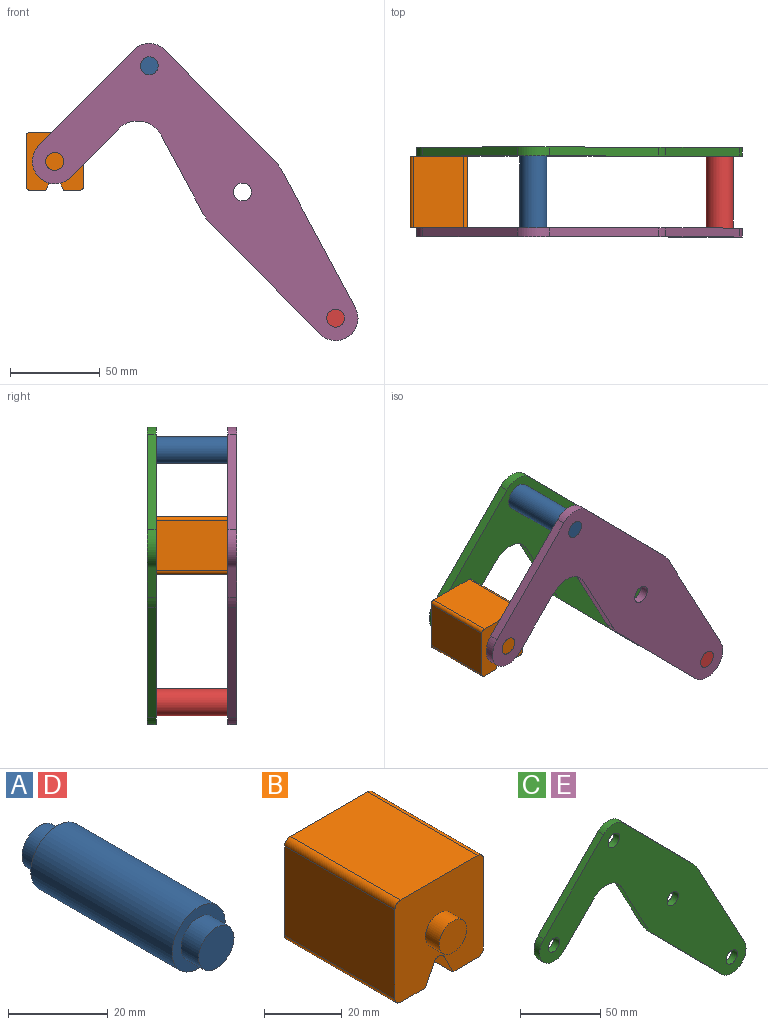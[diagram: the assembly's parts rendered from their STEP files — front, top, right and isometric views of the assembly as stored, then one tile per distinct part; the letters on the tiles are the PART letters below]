
ASSEMBLY  parts=5 mates=3
PART A: 7 faces, bbox 15x50x15 mm
  f0: cylinder r=7.5mm len=40mm, axis (0,-1,0), area 1885mm2, adj f2,f5
  f1: cylinder r=5mm len=10mm, axis (0,1,0), area 157.1mm2, adj f2,f3
  f2: plane 15x15mm, normal (0,-1,0), area 98.2mm2, adj f0,f1
  f3: plane 10x10mm, normal (0,-1,0), area 78.5mm2, adj f1
  f4: cylinder r=5mm len=10mm, axis (0,-1,0), area 157.1mm2, adj f5,f6
  f5: plane 15x15mm, normal (0,1,0), area 98.2mm2, adj f0,f4
  f6: plane 10x10mm, normal (0,1,0), area 78.5mm2, adj f4
PART B: 18 faces, bbox 32.1x50x32.1 mm
  f0: plane 40x28.08mm, normal (1,0,0), area 1123.1mm2, adj f4,f10,f13,f14
  f1: plane 40x9.04mm, normal (0,0,-1), area 361.6mm2, adj f2,f4,f10,f14
  f2: plane 40x6.42mm, normal (-0.89,0,-0.45), area 287.2mm2, adj f1,f4,f10,f15
  f3: plane 40x6.42mm, normal (0.89,0,-0.45), area 287.2mm2, adj f4,f5,f10,f15
  f4: plane 32.08x32.08mm, normal (0,-1,0), area 900.6mm2, adj f0,f1,f2,f3,f5,f6,f7,f9
  f5: plane 40x9.04mm, normal (0,0,-1), area 361.6mm2, adj f3,f4,f10,f16
  f6: plane 40x28.08mm, normal (0,0,1), area 1123.1mm2, adj f4,f10,f13,f17
  f7: plane 40x28.08mm, normal (-1,0,0), area 1123.1mm2, adj f4,f10,f16,f17
  f8: plane 10x10mm, normal (0,-1,0), area 78.5mm2, adj f9
  f9: cylinder r=5mm len=10mm, axis (0,1,0), area 157.1mm2, adj f4,f8
  f10: plane 32.08x32.08mm, normal (0,1,0), area 900.6mm2, adj f0,f1,f2,f3,f5,f6,f7,f12
  f11: plane 10x10mm, normal (0,1,0), area 78.5mm2, adj f12
  f12: cylinder r=5mm len=10mm, axis (0,-1,0), area 157.1mm2, adj f10,f11
  f13: cylinder r=2mm len=40mm, axis (0,1,0), area 125.7mm2, adj f0,f4,f6,f10
  f14: cylinder r=2mm len=40mm, axis (0,-1,0), area 125.7mm2, adj f0,f1,f4,f10
  f15: cylinder r=2mm len=40mm, axis (0,1,0), area 177.1mm2, adj f2,f3,f4,f10
  f16: cylinder r=2mm len=40mm, axis (0,1,0), area 125.7mm2, adj f4,f5,f7,f10
  f17: cylinder r=2mm len=40mm, axis (0,-1,0), area 125.7mm2, adj f4,f6,f7,f10
PART C: 18 faces, bbox 181.7x5x165.8 mm
  f0: plane 43.49x23.35mm, normal (-0.88,0,-0.47), area 246.8mm2, adj f1,f14,f16,f17
  f1: cylinder r=25mm len=5.75mm, axis (0,1,0), area 35.8mm2, adj f0,f2,f16,f17
  f2: plane 61.6x60.87mm, normal (-0.71,0,-0.7), area 433mm2, adj f1,f3,f16,f17
  f3: cylinder r=12.5mm len=21.39mm, axis (0,1,0), area 178.4mm2, adj f2,f4,f16,f17
  f4: plane 76.3x40.96mm, normal (0.88,0,0.47), area 433mm2, adj f3,f5,f16,f17
  f5: cylinder r=25mm len=5.75mm, axis (0,1,0), area 35.8mm2, adj f4,f6,f16,f17
  f6: plane 61.6x60.87mm, normal (0.71,0,0.7), area 433mm2, adj f5,f7,f16,f17
  f7: cylinder r=12.5mm len=17.78mm, axis (0,1,0), area 98.9mm2, adj f6,f8,f16,f17
  f8: plane 53.35x52.71mm, normal (-0.71,0,0.7), area 375mm2, adj f7,f9,f16,f17
  f9: cylinder r=12.5mm len=21.39mm, axis (0,1,0), area 196.3mm2, adj f8,f10,f16,f17
  f10: plane 26.86x26.54mm, normal (0.71,0,-0.7), area 188.8mm2, adj f9,f14,f16,f17
  f11: cylinder r=5mm len=10mm, axis (0,1,0), area 157.1mm2, adj f16,f17
  f12: cylinder r=5mm len=10mm, axis (0,1,0), area 157.1mm2, adj f16,f17
  f13: cylinder r=5mm len=10mm, axis (0,1,0), area 157.1mm2, adj f16,f17
  f14: cylinder r=15mm len=23.89mm, axis (0,1,0), area 140.2mm2, adj f0,f10,f16,f17
  f15: cylinder r=5mm len=10mm, axis (0,1,0), area 157.1mm2, adj f16,f17
  f16: plane 181.66x165.78mm, normal (0,-1,0), area 8710.1mm2, adj f0,f1,f2,f3,f4,f5,f6,f7
  f17: plane 181.66x165.78mm, normal (0,1,0), area 8710.1mm2, adj f0,f1,f2,f3,f4,f5,f6,f7
PART D: same geometry as A
PART E: same geometry as C
PLACE A t=(0,-20,0)mm
PLACE B t=(0,-20,0)mm
PLACE C t=(0,25,0)mm
PLACE D t=(103.95,-20,-140.78)mm
PLACE E t=(0,-20,0)mm fixed
MATE fastened D.f0 <-> E.f3  axis (0,-1,0) through (51.98,-20,-70.39)mm
MATE fastened C.f7 <-> A.f0  axis (0,-1,0) through (-51.98,20,70.39)mm
MATE revolute B.f9 <-> E.f9  axis (0,1,0) through (-104.69,-20,17.04)mm
